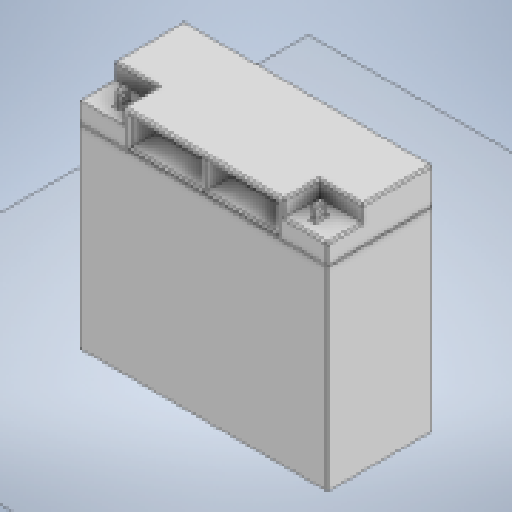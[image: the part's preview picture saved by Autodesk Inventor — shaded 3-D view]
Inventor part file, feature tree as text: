
AUTODESK INVENTOR PART (.ipt)
format: ipt  version: 2023 (Build 270158000, 158)  size: 192,000 bytes
history: native  units: in
note: dims shown in document units (in); Inventor stores cm internally (conversion verified against a paired STEP export)
features: fillet x1
ambient origin geometry x8: Origin, YZ Plane, XZ Plane, XY Plane, X Axis, Y Axis, Z Axis, Center Point
bodies: Solid1 (feature_tree)
feature tree (1):
  fillet  "Fillet4"  [1 undecoded]
note: 1 required parameter value undecoded (feature->parameter linkage not recoverable at this tier; creation-order binding heuristic only, values carry confidence <= 0.55)
